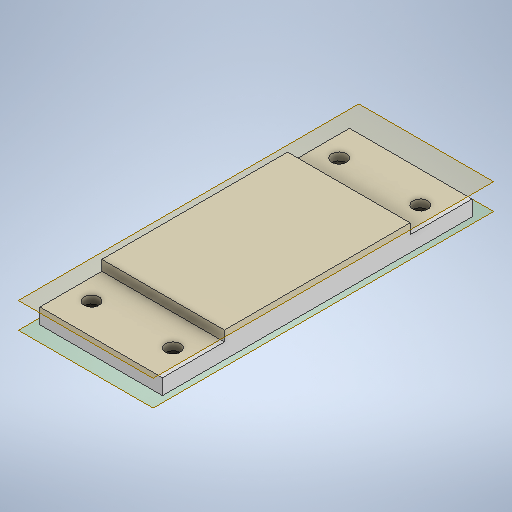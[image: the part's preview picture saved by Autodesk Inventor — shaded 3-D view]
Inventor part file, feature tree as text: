
AUTODESK INVENTOR PART (.ipt)
format: ipt  version: 2025.2 (Build 292293000, 293)  size: 301,056 bytes
history: native  units: mm
features: sketch x4, other x3, extrude x3, hole x1
ambient origin geometry x8: Origin, YZ Plane, XZ Plane, XY Plane, X Axis, Y Axis, Z Axis, Center Point
bodies: Body1 (feature_tree)
feature tree (11):
  other  "ソリッド1"
  extrude  "押し出し1"  Depth=47.5mm
  other  "作業平面1"
  extrude  "押し出し2"  Depth=120.0mm
  other  "作業平面2"
  hole  "穴1"  [1 undecoded]
  extrude  "押し出し3"  TaperAngle=0.0deg  [1 undecoded]
  sketch  "スケッチ1"
  sketch  "スケッチ2"
  sketch  "スケッチ3"
  sketch  "スケッチ4"
note: 2 required parameter values undecoded (feature->parameter linkage not recoverable at this tier; creation-order binding heuristic only, values carry confidence <= 0.55)
